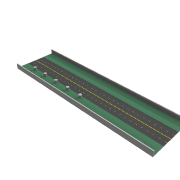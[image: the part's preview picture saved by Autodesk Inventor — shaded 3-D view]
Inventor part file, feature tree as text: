
AUTODESK INVENTOR PART (.ipt)
format: ipt  version: 2021 (Build 250183000, 183)  size: 613,888 bytes
history: native  units: in
note: dims shown in document units (in); Inventor stores cm internally (conversion verified against a paired STEP export)
features: projected_geometry x21, extrude x18, sketch x18, mirror x4, pattern_linear x3, chamfer x2, plane x1
ambient origin geometry x8: Origin, YZ Plane, XZ Plane, XY Plane, X Axis, Y Axis, Z Axis, Center Point
bodies: Solid1 (feature_tree)
feature tree (67):
  extrude  "Extrusion1"  Depth=3937.0079in
  extrude  "Extrusion2"  Depth=472.4409in
  extrude  "Extrusion3"  Depth=118.1102in
  extrude  "Extrusion4"  Depth=196.8504in TaperAngle=0.0deg
  extrude  "Extrusion5"  Depth=23.622in TaperAngle=0.0deg
  plane  "Work Plane1"
  mirror  "Mirror1"
  chamfer  "Chamfer1"  Distance=1.9685in Angle=45.0deg
  chamfer  "Chamfer2"  Distance=137.7953in Angle=45.0deg
  extrude  "Extrusion6"  Depth=196.8504in TaperAngle=0.0deg
  pattern_linear  "Rectangular Pattern1"  Count1=5  [1 undecoded]
  extrude  "Extrusion7"  TaperAngle=0.0deg  [1 undecoded]
  extrude  "Extrusion8"  Depth=1.0in TaperAngle=0.0deg
  mirror  "Mirror2"
  extrude  "Extrusion9"  Depth=3.937in TaperAngle=0.0deg
  extrude  "Extrusion10"  Depth=3.937in TaperAngle=0.0deg
  extrude  "Extrusion11"  Depth=1.0in TaperAngle=0.0deg
  extrude  "Extrusion12"  Depth=196.8504in
  extrude  "Extrusion13"  Depth=0.01in TaperAngle=0.0deg
  extrude  "Extrusion15"  Depth=36.0in
  extrude  "Extrusion16"  Depth=126.0in
  extrude  "Extrusion17"  Depth=0.0344in
  pattern_linear  "Rectangular Pattern2"  [2 undecoded]
  extrude  "Extrusion18"  [1 undecoded]
  mirror  "Mirror3"
  extrude  "Extrusion19"  [1 undecoded]
  pattern_linear  "Rectangular Pattern3"  [2 undecoded]
  mirror  "Mirror4"
  sketch  "Sketch1"  dims[d0=3937.0079in d1=3937.0079in]
  sketch  "Sketch2"  dims[d2=19.685in d3=0.0in d4=472.4409in]
  projected_geometry  "Projected Loop1"
  sketch  "Sketch3"  dims[d5=433.0709in d6=118.1102in]
  projected_geometry  "Projected Loop2"
  projected_geometry  "Projected Loop3"
  sketch  "Sketch4"  dims[d7=3.937in d8=0.0in d9=196.8504in d10=0.0in]
  projected_geometry  "Projected Loop4"
  sketch  "Sketch5"  dims[d11=196.8504in d12=0.0in d13=23.622in d14=0.0in d15=1.9685in d16=0.125in d17=45.0deg d18=137.7953in d19=0.125in d20=45.0deg]
  projected_geometry  "Projected Loop5"
  sketch  "Sketch6"  dims[d21=78.7402in d24=196.8504in d25=0.0in d26=1.9685in d28=393.7008in]
  projected_geometry  "Projected Loop6"
  sketch  "Sketch7"  dims[d29=118.1102in d30=0.0in d31=0.0in d32=0.0in]
  projected_geometry  "Projected Loop7"
  sketch  "Sketch8"  dims[d33=1.0in d34=0.0in d35=1.0in d36=0.0in]
  sketch  "Sketch9"  dims[d37=1.0in d38=0.0in d39=3.937in d40=0.0in]
  projected_geometry  "Projected Loop8"
  sketch  "Sketch10"  dims[d41=3.937in d42=0.0in d45=1.0in d46=0.0in]
  projected_geometry  "Projected Loop9"
  sketch  "Sketch11"  dims[d47=0.0in d48=0.0in d49=1.0in d50=0.0in]
  projected_geometry  "Projected Loop10"
  sketch  "Sketch12"  dims[d51=3.937in d53=196.8504in d54=2.0in]
  projected_geometry  "Projected Loop11"
  projected_geometry  "Projected Loop12"
  projected_geometry  "Projected Loop13"
  projected_geometry  "Projected Loop14"
  sketch  "Sketch13"  dims[d55=4.0in d56=0.01in d57=0.0in]
  projected_geometry  "Projected Loop15"
  sketch  "Sketch15"  dims[d58=4.0in d59=36.0in]
  projected_geometry  "Projected Loop17"
  sketch  "Sketch16"  dims[d60=0.01in d61=0.0in d62=12.2047in d64=126.0in]
  projected_geometry  "Projected Loop18"
  projected_geometry  "Projected Loop19"
  sketch  "Sketch17"  dims[d65=0.5in d66=0.0344in]
  projected_geometry  "Projected Loop20"
  sketch  "Sketch18"  dims[d67=0.5in]
  projected_geometry  "Projected Loop21"
  sketch  "Sketch19"  dims[d68=0.0344in]
  projected_geometry  "Projected Loop22"
note: 8 required parameter values undecoded (feature->parameter linkage not recoverable at this tier; creation-order binding heuristic only, values carry confidence <= 0.55)
